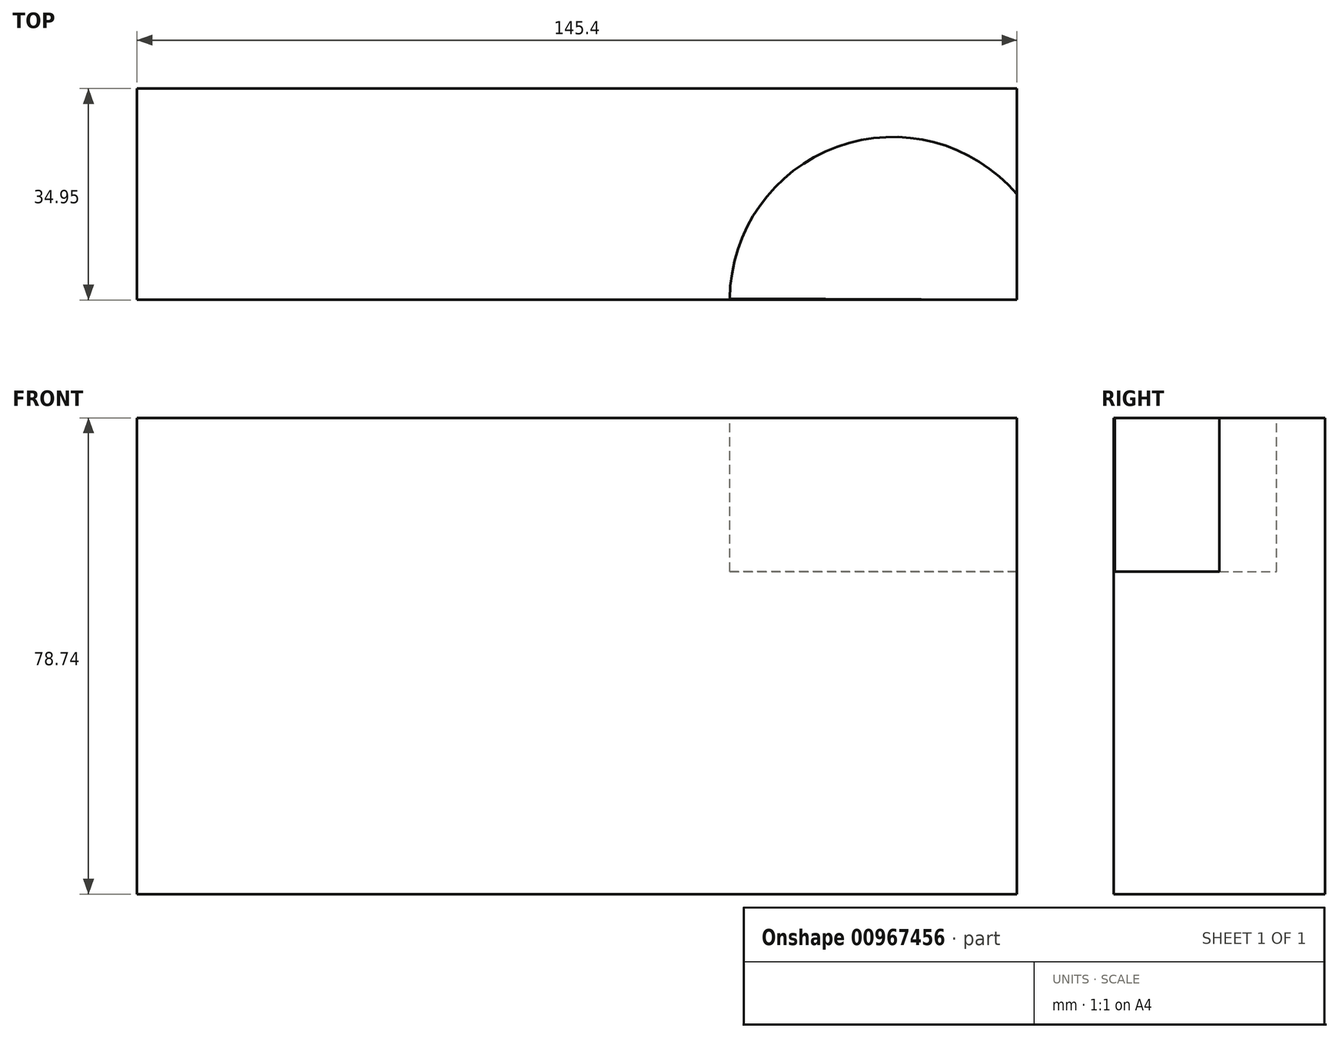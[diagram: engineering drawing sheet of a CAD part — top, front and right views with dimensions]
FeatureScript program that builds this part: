
annotation { "Feature Type Name" : "Feature", "Feature Type Description" : "" }
export const myFeature = defineFeature(function(context is Context, id is Id, definition is map)
    precondition{}
    {
        {
            var Q0;
            Q0=qCreatedBy(makeId("Top.planeOp"),FACE);
            var sketch = newSketch(context, id + "F0", { "sketchPlane" : qUnion([Q0])});
            skLineSegment(sketch, "E0.bottom", {"start": v(145.4, 54.54) * mm, "end": v(0, 54.54) * mm});
            skLineSegment(sketch, "E0.top", {"start": v(145.4, 89.49) * mm, "end": v(0, 89.49) * mm});
            skLineSegment(sketch, "E0.left", {"start": v(145.4, 54.54) * mm, "end": v(145.4, 89.49) * mm});
            skLineSegment(sketch, "E0.right", {"start": v(0, 54.54) * mm, "end": v(0, 89.49) * mm});
            skSolve(sketch);
        }
        {
            var Q0;
            Q0=makeQuery(id+"F0.imprint","IMPRINT",FACE,{"disambiguationData":[TD([[makeQuery(id+"F0.imprint","IMPRINT",EDGE,{"derivedFrom":sQuery(id+"F0.wireOp",EDGE,"E0.bottom")}),-1.0]])]});
            extrude(context, id + "F1", {"entities" : qUnion([Q0]), "depth" : 78.74 * mm, "offsetDistance" : 25.4 * mm});
        }
        {
            var Q0;
            Q0=makeQuery(id+"F1.opExtrude","SWEPT_FACE",FACE,{"disambiguationData":[OSD([sQuery(id+"F0.wireOp",EDGE,"E0.bottom")])]});
            var sketch = newSketch(context, id + "F2", { "sketchPlane" : qUnion([Q0])});
            skCircle(sketch, "E1", {"center": v(73.63, 35.73) * mm, "radius": 17.46 * mm});
            skSolve(sketch);
        }
        {
            var Q0;
            Q0=sQuery(id+"F2.wireOp",EDGE,"E1");
            extrude(context, id + "F3", {"bodyType" : ToolBodyType.SURFACE, "surfaceEntities" : qUnion([Q0]), "depth" : 130.62 * mm, "offsetDistance" : 25.4 * mm});
        }
        {
            var Q0;
            Q0=makeQuery(id+"F1.opExtrude","CAP_FACE",FACE,{"disambiguationData":[OSD([sQuery(id+"F0.wireOp",EDGE,"E0.bottom"),sQuery(id+"F0.wireOp",EDGE,"E0.top"),sQuery(id+"F0.wireOp",EDGE,"E0.left"),sQuery(id+"F0.wireOp",EDGE,"E0.right")])],"isStart":false});
            var sketch = newSketch(context, id + "F4", { "sketchPlane" : qUnion([Q0])});
            skArc(sketch, "E2", {"start": v(145.4, 72.02) * mm, "mid": v(115.7, 79.86) * mm, "end": v(97.97, 54.75) * mm});
            skLineSegment(sketch, "E3", {"start": v(97.97, 54.75) * mm, "end": v(145.4, 54.54) * mm});
            skLineSegment(sketch, "E4", {"start": v(145.4, 54.54) * mm, "end": v(145.4, 72.02) * mm});
            skSolve(sketch);
        }
        {
            var Q0;
            Q0 = qSketchRegion(id + "F4", true);
            extrude(context, id + "F5", {"entities" : qUnion([Q0]), "operationType" : NewBodyOperationType.REMOVE, "oppositeDirection" : true, "depth" : 25.4 * mm, "offsetDistance" : 25.4 * mm});
        }
    });
